# Revit family: GI_TR
name_source: partatom
category: Generic Models
units: mm (PartAtom-declared; Revit-internal decimal feet)

## family parameters
Can host rebar = No
Cut with Voids When Loaded = No
Maintain Annotation Orientation = No
Part Type = Normal
Room Calculation Point = No
Round Connector Dimension = Use Diameter
Shared = No

## types (18) — shared parameters
Description = Zelfdragende goot
Manufacturer = Meilof Riks B.V.
URL = https://www.meilofriks.nl
zero-valued in all types: Default Elevation

## per-type parameters (varying)
| type | Achterzijde_hoogte | Diepte | Diepte_bak | Voorzijde_hoogte |
| GI S280A | 197 mm | 280 mm  [stored 0.918635 ft] | 87 mm  [stored 0.285433 ft] | 185 mm  [stored 0.606955 ft] |
| GI S280B | 222 mm | 280 mm  [stored 0.918635 ft] | 78 mm  [stored 0.255906 ft] | 210 mm  [stored 0.688976 ft] |
| GI S280C | 247 mm | 280 mm  [stored 0.918635 ft] | 78 mm  [stored 0.255906 ft] | 235 mm  [stored 0.770997 ft] |
| GI S310A | 179 mm  [stored 0.58727 ft] | 310 mm  [stored 1.01706 ft] | 74 mm  [stored 0.242782 ft] | 171 mm  [stored 0.561024 ft] |
| GI S310B | 229 mm | 310 mm  [stored 1.01706 ft] | 74 mm  [stored 0.242782 ft] | 221 mm  [stored 0.725066 ft] |
| GI S310C | 279 mm | 310 mm  [stored 1.01706 ft] | 74 mm  [stored 0.242782 ft] | 271 mm  [stored 0.889108 ft] |
| GI S365A | 204 mm | 365 mm  [stored 1.19751 ft] | 95 mm | 193 mm  [stored 0.633202 ft] |
| GI S365B | 254 mm | 365 mm  [stored 1.19751 ft] | 95 mm | 243 mm |
| GI S365C | 304 mm  [stored 0.997375 ft] | 365 mm  [stored 1.19751 ft] | 95 mm | 293 mm |
| GI S400A | 186 mm  [stored 0.610236 ft] | 400 mm  [stored 1.31234 ft] | 78 mm  [stored 0.255906 ft] | 174 mm  [stored 0.570866 ft] |
| GI S400B | 236 mm | 400 mm  [stored 1.31234 ft] | 78 mm  [stored 0.255906 ft] | 224 mm  [stored 0.734908 ft] |
| GI S400C | 286 mm  [stored 0.93832 ft] | 400 mm  [stored 1.31234 ft] | 78 mm  [stored 0.255906 ft] | 274 mm  [stored 0.89895 ft] |
| GI S450A | 192 mm  [stored 0.629921 ft] | 450 mm  [stored 1.47638 ft] | 95 mm | 218 mm  [stored 0.715223 ft] |
| GI S450B | 268 mm | 450 mm  [stored 1.47638 ft] | 95 mm | 242 mm  [stored 0.793963 ft] |
| GI S450C | 318 mm  [stored 1.04331 ft] | 450 mm  [stored 1.47638 ft] | 95 mm | 292 mm  [stored 0.958005 ft] |
| GI S500A | 186 mm  [stored 0.610236 ft] | 500 mm | 78 mm  [stored 0.255906 ft] | 174 mm  [stored 0.570866 ft] |
| GI S500B | 236 mm | 500 mm | 78 mm  [stored 0.255906 ft] | 224 mm  [stored 0.734908 ft] |
| GI S500C | 286 mm  [stored 0.93832 ft] | 500 mm | 78 mm  [stored 0.255906 ft] | 274 mm  [stored 0.89895 ft] |

note: column(s) folded — value = type name in every type: Model

note: [stored X ft] marks values corroborated as IEEE doubles in the binary element streams (Revit-internal decimal feet)

## geometry (parser evidence)
native form markers: Sweep x11
no freeform markers — native parametric forms only
